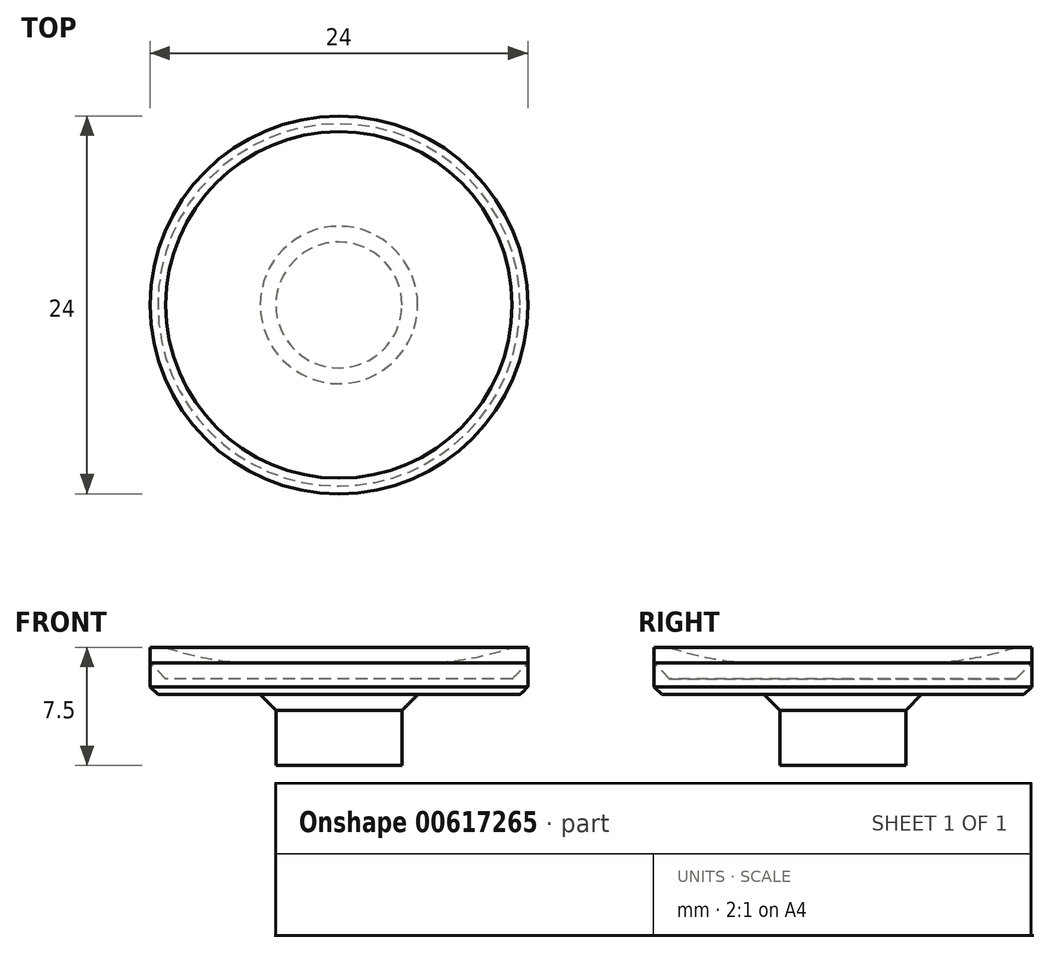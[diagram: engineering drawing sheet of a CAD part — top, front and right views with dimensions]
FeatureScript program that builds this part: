
annotation { "Feature Type Name" : "Feature", "Feature Type Description" : "" }
export const myFeature = defineFeature(function(context is Context, id is Id, definition is map)
    precondition{}
    {
        {
            var Q0;
            Q0=qCreatedBy(makeId("Front.planeOp"),FACE);
            var sketch = newSketch(context, id + "F0", { "sketchPlane" : qUnion([Q0])});
            skLineSegment(sketch, "E0", {"start": v(0, 0) * mm, "end": v(4, 0) * mm});
            skLineSegment(sketch, "E1", {"start": v(4, 0) * mm, "end": v(4, 3.5) * mm});
            skLineSegment(sketch, "E2", {"start": v(4, 3.5) * mm, "end": v(5, 4.5) * mm});
            skLineSegment(sketch, "E3", {"start": v(5, 4.5) * mm, "end": v(12, 4.5) * mm});
            skLineSegment(sketch, "E4", {"start": v(12, 4.5) * mm, "end": v(12, 6.5) * mm});
            skLineSegment(sketch, "E5", {"start": v(0, 5.5) * mm, "end": v(0, 0) * mm});
            skLineSegment(sketch, "E6", {"start": v(12, 6.5) * mm, "end": v(12, 6.5) * mm});
            skLineSegment(sketch, "E7", {"start": v(11, 5.5) * mm, "end": v(0, 5.5) * mm});
            skLineSegment(sketch, "E8", {"start": v(0, 5.5) * mm, "end": v(0, 6.5) * mm});
            skLineSegment(sketch, "E9", {"start": v(12, 6.5) * mm, "end": v(11, 5.5) * mm});
            skLineSegment(sketch, "E10", {"start": v(12, 6.5) * mm, "end": v(12, 7.5) * mm});
            skLineSegment(sketch, "E11", {"start": v(12, 7.5) * mm, "end": v(11, 7.5) * mm});
            skLineSegment(sketch, "E12", {"start": v(0, 6.5) * mm, "end": v(5, 6.5) * mm});
            skArc(sketch, "E13", {"start": v(5, 6.5) * mm, "mid": v(8.04, 6.75) * mm, "end": v(11, 7.5) * mm});
            skSolve(sketch);
        }
        {
            var Q0;
            Q0=makeQuery(id+"F0.imprint","IMPRINT",FACE,{"disambiguationData":[TD([[makeQuery(id+"F0.imprint","IMPRINT",EDGE,{"derivedFrom":sQuery(id+"F0.wireOp",EDGE,"E0")}),1.0]])]});
            var Q1;
            Q1=makeQuery(id+"F0.imprint","IMPRINT",FACE,{"disambiguationData":[TD([[makeQuery(id+"F0.imprint","IMPRINT",EDGE,{"derivedFrom":sQuery(id+"F0.wireOp",EDGE,"8oDHqX6i-wsKN-9OYi-xL7f-mJhccouFAabg")}),1.0]])]});
            var Q2;
            Q2=sQuery(id+"F0.wireOp",EDGE,"E5");
            revolve(context, id + "F1", {"entities" : qUnion([Q0, Q1]), "axis" : qUnion([Q2]), "revolveType" : RevolveType.FULL});
        }
        {
            var Q0;
            Q0=makeQuery(id+"F0.imprint","IMPRINT",FACE,{"disambiguationData":[TD([[makeQuery(id+"F0.imprint","IMPRINT",EDGE,{"derivedFrom":sQuery(id+"F0.wireOp",EDGE,"gh4y3eQA-5Ame-6t6S-D0uh-E9GGQh7ALoIJ")}),-1.0]])]});
            var Q1;
            Q1=makeQuery(id+"F0.imprint","IMPRINT",FACE,{"disambiguationData":[TD([[makeQuery(id+"F0.imprint","IMPRINT",EDGE,{"derivedFrom":sQuery(id+"F0.wireOp",EDGE,"E7")}),-1.0]])]});
            var Q2;
            Q2=sQuery(id+"F0.wireOp",EDGE,"E5");
            revolve(context, id + "F2", {"entities" : qUnion([Q0, Q1]), "axis" : qUnion([Q2]), "revolveType" : RevolveType.FULL});
        }
        {
            var Q0;
            Q0=makeQuery(id+"F1.opRevolve","SWEPT_EDGE",EDGE,{"disambiguationData":[OSD([sQuery(id+"F0.wireOp",EDGE,"E4"),sQuery(id+"F0.wireOp",EDGE,"E6")])]});
            chamfer(context, id + "F3", {"entities" : qUnion([Q0]), "width" : 0.5 * mm, "tangentPropagation" : true});
        }
    });
